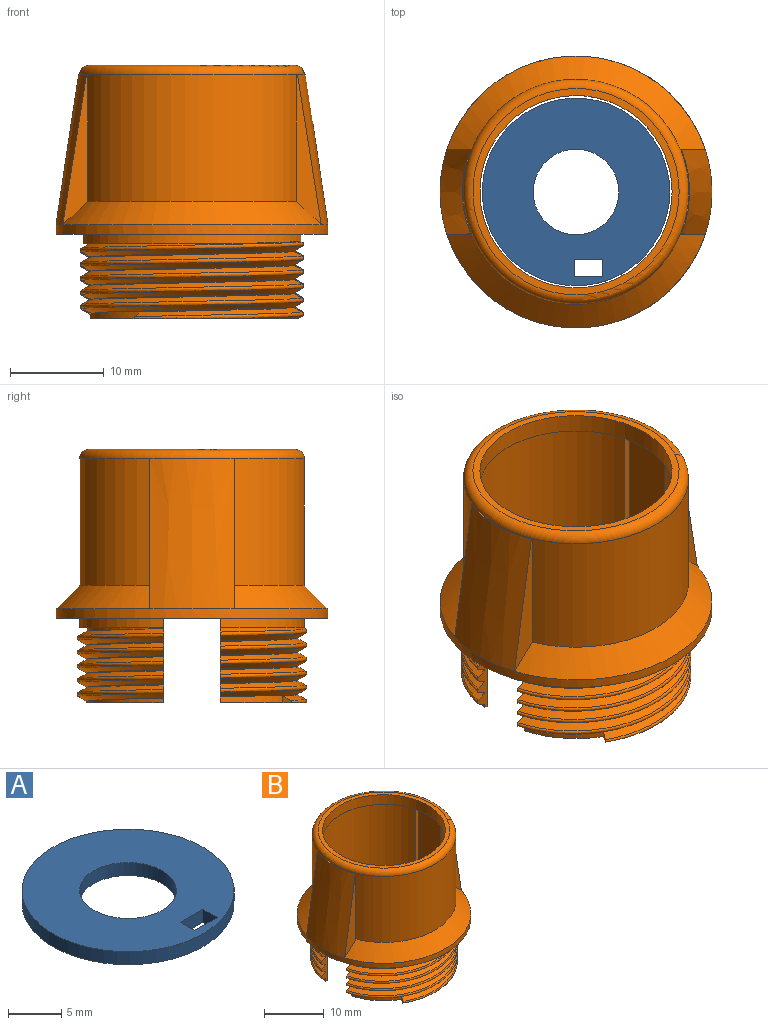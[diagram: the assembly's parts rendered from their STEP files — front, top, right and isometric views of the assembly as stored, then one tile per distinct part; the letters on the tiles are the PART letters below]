
ASSEMBLY  parts=2 mates=2
PART A: 8 faces, bbox 20x20x1.5 mm
  f0: plane 3x1.5mm, normal (0,1,0), area 4.5mm2, adj f1,f4,f6,f7
  f1: plane 1.9x1.5mm, normal (1,0,0), area 2.9mm2, adj f0,f2,f6,f7
  f2: plane 3x1.5mm, normal (0,-1,0), area 4.5mm2, adj f1,f4,f6,f7
  f3: cylinder r=4.56mm len=9.13mm, axis (0,0,-1), area 43mm2, adj f6,f7
  f4: plane 1.9x1.5mm, normal (-1,0,0), area 2.9mm2, adj f0,f2,f6,f7
  f5: cylinder r=10mm len=20mm, axis (0,0,-1), area 94.2mm2, adj f6,f7
  f6: plane 20x20mm, normal (0,0,1), area 243.1mm2, adj f0,f1,f2,f3,f4,f5
  f7: plane 20x20mm, normal (0,0,-1), area 243.1mm2, adj f0,f1,f2,f3,f4,f5
PART B: 97 faces, bbox 29.1x29.1x27.8 mm
  f0: cylinder r=12mm len=22.25mm, axis (0,0,-1), area 384.4mm2, adj f3,f76,f90,f93
  f1: cone r=14.5mm half-angle=45deg, axis (0,0,-1), area 114.5mm2, adj f2,f77,f89,f92
  f2: cylinder r=12mm len=22.25mm, axis (0,0,-1), area 384.4mm2, adj f1,f76,f89,f92
  f3: cone r=14.5mm half-angle=45deg, axis (0,0,-1), area 114.5mm2, adj f0,f77,f90,f93
  f4: bspline ~25x14.43mm, area 29.7mm2, adj f5,f8,f9,f83
  f5: bspline ~22.58x13.03mm, area 2.5mm2, adj f4,f8,f9,f43
  f6: bspline ~22.58x13.03mm, area 2.5mm2, adj f7,f8,f9,f10
  f7: bspline ~25x14.43mm, area 29.7mm2, adj f6,f8,f9,f83
  f8: plane 25.06x1.57mm, normal (0,-1,0), area 21.3mm2, adj f4,f5,f6,f7,f10,f29,f30,f31
  f9: plane 25.06x1.57mm, normal (0,-1,0), area 21.4mm2, adj f4,f5,f6,f7,f10,f28,f29,f30
  f10: cylinder r=11.2mm len=21.58mm, axis (0,0,-1), area 2.9mm2, adj f6,f8,f9,f35
  f11: bspline ~25x14.43mm, area 29.7mm2, adj f12,f15,f16,f82
  f12: bspline ~22.58x13.03mm, area 2.5mm2, adj f11,f15,f16,f22
  f13: bspline ~22.58x13.03mm, area 2.5mm2, adj f14,f15,f16,f17
  f14: bspline ~25x14.43mm, area 29.7mm2, adj f13,f15,f16,f82
  f15: plane 25.06x1.57mm, normal (0,1,0), area 21.9mm2, adj f11,f12,f13,f14,f17,f18,f19,f20
  f16: plane 25.06x1.57mm, normal (0,1,0), area 21.4mm2, adj f11,f12,f13,f14,f17,f18,f19,f20
  f17: cylinder r=11.2mm len=21.58mm, axis (0,0,-1), area 2.9mm2, adj f13,f15,f16,f50
  f18: bspline ~25x14.43mm, area 29.7mm2, adj f15,f16,f19,f80
  f19: bspline ~22.58x13.03mm, area 2.5mm2, adj f15,f16,f18,f27
  f20: bspline ~22.58x13.03mm, area 2.5mm2, adj f15,f16,f21,f22
  f21: bspline ~25x14.43mm, area 29.7mm2, adj f15,f16,f20,f80
  f22: cylinder r=11.2mm len=21.58mm, axis (0,0,-1), area 2.9mm2, adj f12,f15,f16,f20
  f23: bspline ~25x14.43mm, area 12.4mm2, adj f15,f16,f26,f75,f78
  f24: bspline ~22.58x13.03mm, area 2.5mm2, adj f15,f16,f25,f27
  f25: bspline ~25x14.43mm, area 29.7mm2, adj f15,f16,f24,f78
  f26: cylinder r=12mm len=23.24mm, axis (0,0,-1), area 30.3mm2, adj f15,f16,f23,f64,f75
  f27: cylinder r=11.2mm len=21.58mm, axis (0,0,-1), area 2.9mm2, adj f15,f16,f19,f24
  f28: bspline ~22.58x13.03mm, area 2mm2, adj f9,f29,f32,f33
  f29: bspline ~25x14.43mm, area 28.8mm2, adj f8,f9,f28,f32,f87
  f30: bspline ~25x14.43mm, area 29.7mm2, adj f8,f9,f31,f87
  f31: bspline ~22.58x13.03mm, area 2.5mm2, adj f8,f9,f30,f38
  f32: plane 21.99x8.26mm, normal (0,0,-1), area 12.7mm2, adj f8,f9,f28,f29,f33,f69
  f33: cylinder r=11.2mm len=18.37mm, axis (0,0,-1), area 5.6mm2, adj f9,f28,f32
  f34: bspline ~25x14.43mm, area 29.7mm2, adj f8,f9,f35,f85
  f35: bspline ~22.58x13.03mm, area 2.5mm2, adj f8,f9,f10,f34
  f36: bspline ~22.58x13.03mm, area 2.5mm2, adj f8,f9,f37,f38
  f37: bspline ~25x14.43mm, area 29.7mm2, adj f8,f9,f36,f85
  f38: cylinder r=11.2mm len=21.58mm, axis (0,0,-1), area 2.9mm2, adj f8,f9,f31,f36
  f39: bspline ~25x14.43mm, area 29.7mm2, adj f8,f9,f40,f81
  f40: bspline ~22.58x13.03mm, area 2.5mm2, adj f8,f9,f39,f48
  f41: bspline ~22.58x13.03mm, area 2.5mm2, adj f8,f9,f42,f43
  f42: bspline ~25x14.43mm, area 29.7mm2, adj f8,f9,f41,f81
  f43: cylinder r=11.2mm len=21.58mm, axis (0,0,-1), area 2.9mm2, adj f5,f8,f9,f41
  f44: bspline ~25x14.43mm, area 29.7mm2, adj f8,f9,f45,f79
  f45: bspline ~22.58x13.03mm, area 2.5mm2, adj f8,f9,f44,f74
  f46: bspline ~22.58x13.03mm, area 2.5mm2, adj f8,f9,f47,f48
  f47: bspline ~25x14.43mm, area 29.7mm2, adj f8,f9,f46,f79
  f48: cylinder r=11.2mm len=21.58mm, axis (0,0,-1), area 2.9mm2, adj f8,f9,f40,f46
  f49: bspline ~25x14.43mm, area 29.7mm2, adj f15,f16,f50,f84
  f50: bspline ~22.58x13.03mm, area 2.5mm2, adj f15,f16,f17,f49
  f51: bspline ~22.58x13.03mm, area 2.5mm2, adj f15,f16,f52,f53
  f52: bspline ~25x14.43mm, area 29.7mm2, adj f15,f16,f51,f84
  f53: cylinder r=11.2mm len=21.58mm, axis (0,0,-1), area 2.9mm2, adj f15,f16,f51,f55
  f54: bspline ~25x14.43mm, area 29.7mm2, adj f15,f16,f55,f86
  f55: bspline ~22.58x13.03mm, area 2.5mm2, adj f15,f16,f53,f54
  f56: bspline ~22.58x13.03mm, area 2.5mm2, adj f15,f16,f57,f58
  f57: bspline ~25x14.43mm, area 29.7mm2, adj f15,f16,f56,f86
  f58: cylinder r=11.2mm len=21.58mm, axis (0,0,-1), area 8.2mm2, adj f15,f16,f56,f59,f61,f63
  f59: plane 0.93x0.72mm, normal (-0.87,0.5,0), area 0.5mm2, adj f58,f61,f62,f63,f88
  f60: bspline ~18.75x14.43mm, area 2.6mm2, adj f15,f63,f88
  f61: bspline ~16.53x8.31mm, area 1.8mm2, adj f15,f58,f59,f62
  f62: bspline ~17.81x9.33mm, area 20.8mm2, adj f15,f59,f61,f88
  f63: plane 22.27x9.35mm, normal (0,0,-1), area 30mm2, adj f15,f16,f58,f59,f60,f73,f88
  f64: plane 29x29mm, normal (0,0,-1), area 217.1mm2, adj f8,f9,f15,f16,f26,f65,f66,f67
  f65: cylinder r=12mm len=23.24mm, axis (0,0,-1), area 31.6mm2, adj f8,f9,f64,f68
  f66: plane 16x6mm, normal (1,0,0), area 96mm2, adj f9,f16,f64,f70
  f67: plane 16x6mm, normal (-1,0,0), area 96mm2, adj f8,f15,f64,f70
  f68: plane 23.24x9mm, normal (0,0,-1), area 24.3mm2, adj f8,f9,f65,f74
  f69: cylinder r=10.8mm len=25mm, axis (0,0,1), area 696.2mm2, adj f8,f9,f32,f70
  f70: plane 22.25x21.6mm, normal (0,0,-1), area 42mm2, adj f8,f9,f15,f16,f66,f67,f69,f71
  f71: cylinder r=10.25mm len=20.5mm, axis (0,0,-1), area 128.8mm2, adj f70,f72
  f72: plane 22x22mm, normal (0,0,1), area 50.1mm2, adj f71,f76
  f73: cylinder r=10.8mm len=25mm, axis (0,0,1), area 696.2mm2, adj f15,f16,f63,f70
  f74: cylinder r=11.2mm len=21.58mm, axis (0,0,-1), area 12.4mm2, adj f8,f9,f45,f68
  f75: plane 15.77x9mm, normal (0,0,-1), area 6.8mm2, adj f16,f23,f26
  f76: torus R=11mm, axis (0,0,1), area 114.8mm2, adj f0,f2,f72,f91,f94
  f77: cylinder r=14.5mm len=29mm, axis (0,0,1), area 91.1mm2, adj f1,f3,f64,f95,f96
  f78: bspline ~24.62x10.37mm, area 16.9mm2, adj f15,f16,f23,f25
  f79: bspline ~24.62x10.37mm, area 16.9mm2, adj f8,f9,f44,f47
  f80: bspline ~24.62x10.37mm, area 16.9mm2, adj f15,f16,f18,f21
  f81: bspline ~24.62x10.37mm, area 16.9mm2, adj f8,f9,f39,f42
  f82: bspline ~24.62x10.37mm, area 16.9mm2, adj f11,f14,f15,f16
  f83: bspline ~24.62x10.37mm, area 16.9mm2, adj f4,f7,f8,f9
  f84: bspline ~24.62x10.37mm, area 16.9mm2, adj f15,f16,f49,f52
  f85: bspline ~24.62x10.37mm, area 16.9mm2, adj f8,f9,f34,f37
  f86: bspline ~24.62x10.37mm, area 16.9mm2, adj f15,f16,f54,f57
  f87: bspline ~24.62x10.37mm, area 16.9mm2, adj f8,f9,f29,f30
  f88: bspline ~18.8x10.16mm, area 10.4mm2, adj f15,f59,f60,f62,f63
  f89: plane 16.09x2.75mm, normal (0,1,0), area 19mm2, adj f1,f2,f91,f95
  f90: plane 16.09x2.75mm, normal (0,-1,0), area 19mm2, adj f0,f3,f91,f95
  f91: plane 9x0.98mm, normal (0,0,1), area 1mm2, adj f76,f89,f90,f95
  f92: plane 16.09x2.75mm, normal (0,1,0), area 19mm2, adj f1,f2,f94,f96
  f93: plane 16.09x2.75mm, normal (0,-1,0), area 19mm2, adj f0,f3,f94,f96
  f94: plane 9x0.98mm, normal (0,0,1), area 1mm2, adj f76,f92,f93,f96
  f95: cone r=14.5mm half-angle=8.5deg, axis (0,0,-1), area 149.5mm2, adj f77,f89,f90,f91
  f96: cone r=14.5mm half-angle=8.5deg, axis (0,0,-1), area 149.5mm2, adj f77,f92,f93,f94
PLACE A t=(-13.88,6.41,5.79)mm
PLACE B t=(-13.88,6.41,20.79)mm
MATE planar A.f7 <-> B.f0  axis (0,0,-1) through (-13.92,6.6,5.79)mm
MATE cylindrical A.f3 <-> B.f0  axis (0,0,1) through (-13.88,6.41,7.29)mm
